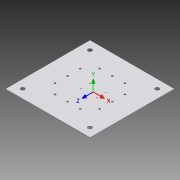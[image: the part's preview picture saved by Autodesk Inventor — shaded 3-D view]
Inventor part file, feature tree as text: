
AUTODESK INVENTOR PART (.ipt)
format: ipt  version: 2015 (Build 190159000, 159)  size: 243,200 bytes
history: native  units: in
note: dims shown in document units (in); Inventor stores cm internally (conversion verified against a paired STEP export)
features: other x10, sketch x5, hole x2, sheet_metal_op x1
ambient origin geometry x8: Origin, YZ Plane, XZ Plane, XY Plane, X Axis, Y Axis, Z Axis, Center Point
bodies: Solid1 (feature_tree)
feature tree (18):
  sheet_metal_op  "Face1"
  other  "UCS1"
  hole  "Hole1"  [1 undecoded]
  hole  "Hole2"  [1 undecoded]
  sketch  "Sketch9"  dims[d39=0.125in d40=0.75in d41=0.75in d42=5.313in d43=6.063in d44=11.376in d45=6.063in d46=0.25in d47=0.0in d48=4.2872in d49=5.9746in d50=6.063in d51=0.25in d52=8.3244in d53=4.2872in d54=0.125in d55=8.4494in d56=0.0625in d57=10.0in d58=10.0in d59=0.125in d60=8.0in d61=0.5in d62=0.5in d63=0.5in d64=0.5in d65=0.125in d66=0.0in d70=-2.5491in d71=0.0in d72=3.032in d73=0.0in d74=0.0in d75=0.0in d76=0.14in d77=0.75in d78=0.375in d79=0.25in d80=0.5635in d81=0.125in d82=0.8108in d83=0.144in d84=0.75in d85=0.279in d86=0.25in d87=0.5635in d88=0.125in d89=0.8108in d90=3.6662in d91=4.4695in]
  sketch  "Sketch1"  dims[d1=0.7874in d3=0.7874in d5=0.7874in d7=0.7874in d9=0.7874in d11=0.7874in d13=0.7874in d15=0.7874in d16=0.75in d17=0.75in d18=0.75in d19=0.75in d20=0.25in d21=0.25in d22=0.25in d23=0.25in d24=2.5681in d25=0.375in d26=1.5in d27=1.5in d28=1.5in d29=1.5in d30=1.5in d31=1.5in d32=1.5in d33=1.5in d34=90.0deg]
  other  "Plate1"
  sketch  "Sketch2"  dims[d35=45.0deg d36=90.0deg]
  sketch  "Sketch7"  dims[d37=90.0deg]
  sketch  "Sketch8"  dims[d38=90.0deg]
  other  "Cut1"
  other  "UCS1: YZ Plane"
  other  "UCS1: XZ Plane"
  other  "UCS1: XY Plane"
  other  "UCS1: X Axis"
  other  "UCS1: Y Axis"
  other  "UCS1: Z Axis"
  other  "UCS1: Center Point"
note: 2 required parameter values undecoded (feature->parameter linkage not recoverable at this tier; creation-order binding heuristic only, values carry confidence <= 0.55)
